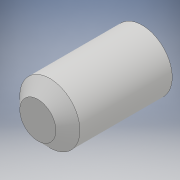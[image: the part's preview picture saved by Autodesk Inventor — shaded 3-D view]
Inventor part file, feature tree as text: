
AUTODESK INVENTOR PART (.ipt)
format: ipt  version: 2018 (Build 220112000, 112)  size: 112,128 bytes
history: native  units: mm
features: extrude x2, sketch x2, chamfer x1
ambient origin geometry x8: Origin, YZ Plane, XZ Plane, XY Plane, X Axis, Y Axis, Z Axis, Center Point
bodies: Solide1 (feature_tree)
feature tree (5):
  extrude  "Extrusion1"  Depth=15.0mm
  extrude  "Extrusion2"  Depth=26.0mm TaperAngle=0.0deg
  chamfer  "Chanfrein1"  Distance=12.0mm
  sketch  "Esquisse1"
  sketch  "Esquisse2"
